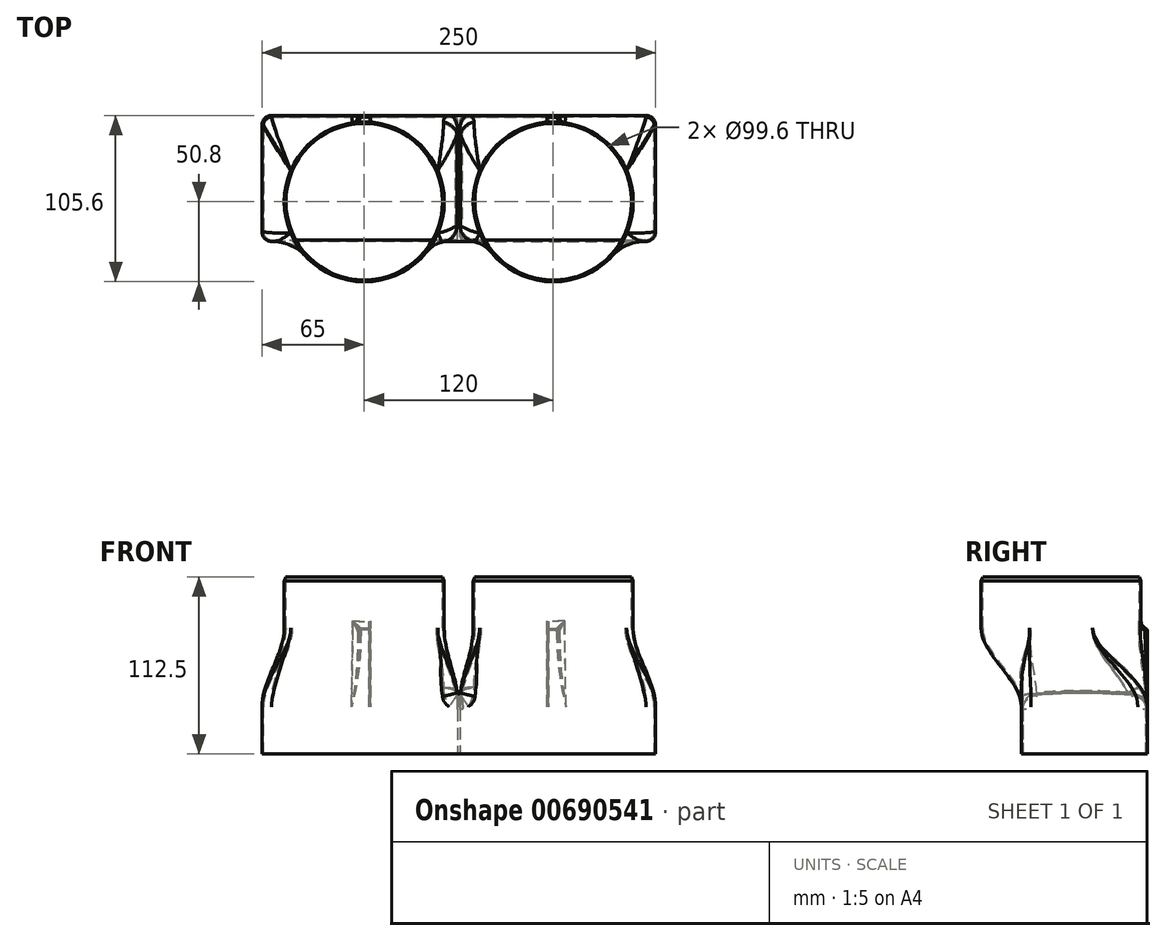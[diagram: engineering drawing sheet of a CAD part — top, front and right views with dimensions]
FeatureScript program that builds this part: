
annotation { "Feature Type Name" : "Feature", "Feature Type Description" : "" }
export const myFeature = defineFeature(function(context is Context, id is Id, definition is map)
    precondition{}
    {
        {
            var Q0;
            Q0=qCreatedBy(makeId("Front.planeOp"),FACE);
            var sketch = newSketch(context, id + "F0", { "sketchPlane" : qUnion([Q0])});
            skLineSegment(sketch, "E0", {"start": v(50.8, 0) * mm, "end": v(50.8, 30) * mm});
            skLineSegment(sketch, "E1", {"start": v(50.8, 30) * mm, "end": v(48.8, 35) * mm});
            skLineSegment(sketch, "E2", {"start": v(48.8, 35) * mm, "end": v(0, 35) * mm});
            skLineSegment(sketch, "E3", {"start": v(0, 35) * mm, "end": v(0, 0) * mm});
            skLineSegment(sketch, "E4", {"start": v(50.8, 0) * mm, "end": v(0, 0) * mm});
            skSolve(sketch);
        }
        {
            var Q0;
            Q0=makeQuery(id+"F0.imprint","IMPRINT",FACE,{"disambiguationData":[TD([[makeQuery(id+"F0.imprint","IMPRINT",EDGE,{"derivedFrom":sQuery(id+"F0.wireOp",EDGE,"E0")}),1.0]])]});
            var Q1;
            Q1=sQuery(id+"F0.wireOp",EDGE,"E3");
            revolve(context, id + "F1", {"entities" : qUnion([Q0]), "axis" : qUnion([Q1]), "revolveType" : RevolveType.FULL});
        }
        {
            var Q0;
            Q0=qCreatedBy(makeId("Right.planeOp"),FACE);
            cPlane(context, id + "F2", {"entities" : qUnion([Q0]), "cplaneType" : CPlaneType.OFFSET, "offset" : 60 * mm, "oppositeDirection" : true, "width" : 150 * mm, "height" : 150 * mm});
        }
        {
            var Q0;
            Q0=qCreatedBy(makeId("Top.planeOp"),FACE);
            cPlane(context, id + "F3", {"entities" : qUnion([Q0]), "cplaneType" : CPlaneType.OFFSET, "offset" : 50 * mm, "oppositeDirection" : true, "width" : 150 * mm, "height" : 150 * mm});
        }
        {
            var Q0;
            Q0=qCreatedBy(id+"F3.planeOp",FACE);
            var sketch = newSketch(context, id + "F4", { "sketchPlane" : qUnion([Q0])});
            skLineSegment(sketch, "E5.bottom", {"start": v(-185, -25.2) * mm, "end": v(65, -25.2) * mm});
            skLineSegment(sketch, "E5.top", {"start": v(-185, 54.8) * mm, "end": v(65, 54.8) * mm});
            skLineSegment(sketch, "E5.left", {"start": v(-185, -25.2) * mm, "end": v(-185, 54.8) * mm});
            skLineSegment(sketch, "E5.right", {"start": v(65, -25.2) * mm, "end": v(65, 54.8) * mm});
            skPoint(sketch, "E5.middle", {"position": v(-60, 14.8) * mm});
            skLineSegment(sketch, "E6", {"start": v(-60, -25.2) * mm, "end": v(-60, 54.8) * mm});
            skSolve(sketch);
        }
        {
            var Q0;
            Q0=qCreatedBy(makeId("Top.planeOp"),FACE);
            var sketch = newSketch(context, id + "F5", { "sketchPlane" : qUnion([Q0])});
            skLineSegment(sketch, "E7.bottom", {"start": v(46.7, -20) * mm, "end": v(-46.7, -20) * mm, "construction": true});
            skLineSegment(sketch, "E7.top", {"start": v(46.7, 20) * mm, "end": v(-46.7, 20) * mm, "construction": true});
            skLineSegment(sketch, "E7.left", {"start": v(46.7, -20) * mm, "end": v(46.7, 20) * mm, "construction": true});
            skLineSegment(sketch, "E7.right", {"start": v(-46.7, -20) * mm, "end": v(-46.7, 20) * mm, "construction": true});
            skPoint(sketch, "E7.middle", {"position": v(0, 0) * mm});
            skArc(sketch, "E8", {"start": v(46.7, -20) * mm, "mid": v(50.8, 0) * mm, "end": v(46.7, 20) * mm});
            skArc(sketch, "E9", {"start": v(46.7, 20) * mm, "mid": v(0, 50.8) * mm, "end": v(-46.7, 20) * mm});
            skArc(sketch, "E10", {"start": v(-46.7, 20) * mm, "mid": v(-50.8, 0) * mm, "end": v(-46.7, -20) * mm});
            skArc(sketch, "E11", {"start": v(-46.7, -20) * mm, "mid": v(0, -50.8) * mm, "end": v(46.7, -20) * mm});
            skSolve(sketch);
        }
        {
            var Q1;
            {var subQ0=sQuery(id+"F4.wireOp",EDGE,"E5.right");Q1=makeQuery(id+"F4.imprint","IMPRINT",FACE,{"disambiguationData":[TD([[makeQuery(id+"F4.imprint","IMPRINT",EDGE,{"derivedFrom":subQ0}),1.0]])]});}
            var Q2;
            Q2 = qSketchRegion(id + "F5", true);
            loft(context, id + "F6", {"operationType" : NewBodyOperationType.ADD, "startCondition" : LoftEndDerivativeType.NORMAL_TO_PROFILE, "startMagnitude" : 1, "endCondition" : LoftEndDerivativeType.NORMAL_TO_PROFILE, "endMagnitude" : 1, "sheetProfilesArray" : [{ "sheetProfileEntities" : qUnion([Q1]) }, { "sheetProfileEntities" : qUnion([Q2]) }]});
        }
        {
            var Q0;
            {var subQ0=sQuery(id+"F4.wireOp",EDGE,"E5.right");Q0=makeQuery(id+"F6.opLoft","CAP_FACE",FACE,{"disambiguationData":[OSD([makeQuery(id+"F4.imprint","IMPRINT",FACE,{"disambiguationData":[TD([[makeQuery(id+"F4.imprint","IMPRINT",EDGE,{"derivedFrom":subQ0}),1.0]])]})])],"isStart":true});}
            extrude(context, id + "F7", {"entities" : qUnion([Q0]), "operationType" : NewBodyOperationType.ADD, "depth" : 30 * mm, "offsetDistance" : 25 * mm});
        }
        {
            var Q0;
            Q0=makeQuery(id+"F7.opExtrude","SWEPT_EDGE",EDGE,{"disambiguationData":[OSD([sQuery(id+"F4.wireOp",EDGE,"E5.bottom"),sQuery(id+"F4.wireOp",EDGE,"E5.right")])]});
            var Q1;
            Q1=makeQuery(id+"F7.opExtrude","SWEPT_EDGE",EDGE,{"disambiguationData":[OSD([sQuery(id+"F4.wireOp",EDGE,"E5.top"),sQuery(id+"F4.wireOp",EDGE,"E5.right")])]});
            fillet(context, id + "F8", {"entities" : qUnion([Q0, Q1]), "radius" : 6 * mm, "tangentPropagation" : true, "allowEdgeOverflow" : false});
        }
        {
            var Q0;
            {var subQ0=makeQuery(id+"F7.opExtrude","SWEPT_FACE",FACE,{"disambiguationData":[OSD([sQuery(id+"F4.wireOp",EDGE,"E5.top"),sQuery(id+"F4.wireOp",EDGE,"E5.right"),sQuery(id+"F4.wireOp",EDGE,"E6")])]});Q0=makeQuery(id+"F15.boolean.opBoolean","MERGE",FACE,{"derivedFrom":[subQ0,makeQuery(id+"F15.opPattern","COPY",FACE,{"derivedFrom":subQ0,"instanceName":"1"})]});}
            var sketch = newSketch(context, id + "F9", { "sketchPlane" : qUnion([Q0])});
            skLineSegment(sketch, "E12.bottom", {"start": v(4, 0) * mm, "end": v(-4, 0) * mm});
            skLineSegment(sketch, "E12.top", {"start": v(4, -50) * mm, "end": v(-4, -50) * mm});
            skLineSegment(sketch, "E12.left", {"start": v(4, 0) * mm, "end": v(4, -50) * mm});
            skLineSegment(sketch, "E12.right", {"start": v(-4, 0) * mm, "end": v(-4, -50) * mm});
            skPoint(sketch, "E12.middle", {"position": v(0, -25) * mm});
            skSolve(sketch);
        }
        {
            var Q0;
            Q0 = qSketchRegion(id + "F9", true);
            var Q1;
            Q1=makeQuery(id+"F6.opLoft","SWEPT_FACE",FACE,{"disambiguationData":[OSD([sQuery(id+"F4.wireOp",EDGE,"E5.top"),sQuery(id+"F4.wireOp",EDGE,"E5.right"),sQuery(id+"F4.wireOp",EDGE,"E6"),sQuery(id+"F5.wireOp",EDGE,"E8"),sQuery(id+"F5.wireOp",EDGE,"E9"),sQuery(id+"F5.wireOp",EDGE,"E10")])]});
            extrude(context, id + "F10", {"entities" : qUnion([Q0]), "operationType" : NewBodyOperationType.ADD, "endBound" : BoundingType.UP_TO_SURFACE, "oppositeDirection" : true, "depth" : 25 * mm, "endBoundEntityFace" : qUnion([Q1]), "offsetDistance" : 25 * mm});
        }
        {
            var Q0;
            Q0=makeQuery(id+"F10.opExtrude","CAP_EDGE",EDGE,{"disambiguationData":[OSD([sQuery(id+"F9.wireOp",EDGE,"E12.bottom")])],"isStart":true});
            fillet(context, id + "F11", {"entities" : qUnion([Q0]), "radius" : 2 * mm, "tangentPropagation" : true, "allowEdgeOverflow" : false});
        }
        {
            var Q0;
            Q0=makeQuery(id+"F10.opExtrude","TWEAK_EDGE",EDGE,{"derivedFrom":[makeQuery(id+"F6.opLoft","SWEPT_FACE",FACE,{"disambiguationData":[OSD([sQuery(id+"F4.wireOp",EDGE,"E5.top"),sQuery(id+"F4.wireOp",EDGE,"E5.right"),sQuery(id+"F4.wireOp",EDGE,"E6"),sQuery(id+"F5.wireOp",EDGE,"E8"),sQuery(id+"F5.wireOp",EDGE,"E9"),sQuery(id+"F5.wireOp",EDGE,"E10")])]}),makeQuery(id+"F9.imprint","IMPRINT",EDGE,{"derivedFrom":sQuery(id+"F9.wireOp",EDGE,"E12.right")})]});
            var Q1;
            Q1=makeQuery(id+"F10.opExtrude","TWEAK_EDGE",EDGE,{"derivedFrom":[makeQuery(id+"F6.opLoft","SWEPT_FACE",FACE,{"disambiguationData":[OSD([sQuery(id+"F4.wireOp",EDGE,"E5.top"),sQuery(id+"F4.wireOp",EDGE,"E5.right"),sQuery(id+"F4.wireOp",EDGE,"E6"),sQuery(id+"F5.wireOp",EDGE,"E8"),sQuery(id+"F5.wireOp",EDGE,"E9"),sQuery(id+"F5.wireOp",EDGE,"E10")])]}),makeQuery(id+"F9.imprint","IMPRINT",EDGE,{"derivedFrom":sQuery(id+"F9.wireOp",EDGE,"E12.left")})]});
            fillet(context, id + "F12", {"entities" : qUnion([Q0, Q1]), "radius" : 4 * mm, "tangentPropagation" : true, "allowEdgeOverflow" : false});
        }
        {
            var Q0;
            {var subQ0=sQuery(id+"F5.wireOp",EDGE,"E10");var subQ1=sQuery(id+"F5.wireOp",EDGE,"E9");var subQ2=sQuery(id+"F5.wireOp",EDGE,"E8");Q0=makeQuery(id+"F10.boolean.opBoolean","MERGE",EDGE,{"derivedFrom":[makeQuery(id+"F6.boolean.opBoolean","MERGE",EDGE,{"derivedFrom":[makeQuery(id+"F1.opRevolve","SWEPT_EDGE",EDGE,{"disambiguationData":[OSD([sQuery(id+"F0.wireOp",EDGE,"E0"),sQuery(id+"F0.wireOp",EDGE,"E4")])]}),makeQuery(id+"F6.opLoft","MID_CAP_EDGE",EDGE,{"disambiguationData":[OSD([subQ2,subQ1,subQ0])],"capPos":1.0})]}),makeQuery(id+"F10.opExtrude","TWEAK_EDGE",EDGE,{"derivedFrom":[makeQuery(id+"F6.opLoft","SWEPT_FACE",FACE,{"disambiguationData":[OSD([sQuery(id+"F4.wireOp",EDGE,"E5.top"),sQuery(id+"F4.wireOp",EDGE,"E5.right"),sQuery(id+"F4.wireOp",EDGE,"E6"),subQ2,subQ1,subQ0])]}),makeQuery(id+"F9.imprint","IMPRINT",EDGE,{"derivedFrom":sQuery(id+"F9.wireOp",EDGE,"E12.bottom")})]})]});}
            fillet(context, id + "F13", {"entities" : qUnion([Q0]), "radius" : 5 * mm, "tangentPropagation" : true, "allowEdgeOverflow" : false});
        }
        {
            var Q0;
            Q0=makeQuery(id+"F12.opFillet","BLEND_EDGE",EDGE,{"blendedFrom":[makeQuery(id+"F10.opExtrude","TWEAK_EDGE",EDGE,{"derivedFrom":[makeQuery(id+"F6.opLoft","SWEPT_FACE",FACE,{"disambiguationData":[OSD([sQuery(id+"F4.wireOp",EDGE,"E5.top"),sQuery(id+"F4.wireOp",EDGE,"E5.right"),sQuery(id+"F4.wireOp",EDGE,"E6"),sQuery(id+"F5.wireOp",EDGE,"E8"),sQuery(id+"F5.wireOp",EDGE,"E9"),sQuery(id+"F5.wireOp",EDGE,"E10")])]}),makeQuery(id+"F9.imprint","IMPRINT",EDGE,{"derivedFrom":sQuery(id+"F9.wireOp",EDGE,"E12.right")})]}),makeQuery(id+"F11.opFillet","BLEND_FACE",FACE,{"disambiguationData":[OSD([sQuery(id+"F9.wireOp",EDGE,"E12.bottom")])]})],"blendedInto":[makeQuery(id+"F11.opFillet","BLEND_FACE",FACE,{"disambiguationData":[OSD([sQuery(id+"F9.wireOp",EDGE,"E12.bottom")])]})]});
            var Q1;
            Q1=makeQuery(id+"F12.opFillet","BLEND_EDGE",EDGE,{"blendedFrom":[makeQuery(id+"F10.opExtrude","TWEAK_EDGE",EDGE,{"derivedFrom":[makeQuery(id+"F6.opLoft","SWEPT_FACE",FACE,{"disambiguationData":[OSD([sQuery(id+"F4.wireOp",EDGE,"E5.top"),sQuery(id+"F4.wireOp",EDGE,"E5.right"),sQuery(id+"F4.wireOp",EDGE,"E6"),sQuery(id+"F5.wireOp",EDGE,"E8"),sQuery(id+"F5.wireOp",EDGE,"E9"),sQuery(id+"F5.wireOp",EDGE,"E10")])]}),makeQuery(id+"F9.imprint","IMPRINT",EDGE,{"derivedFrom":sQuery(id+"F9.wireOp",EDGE,"E12.left")})]}),makeQuery(id+"F11.opFillet","BLEND_FACE",FACE,{"disambiguationData":[OSD([sQuery(id+"F9.wireOp",EDGE,"E12.bottom")])]})],"blendedInto":[makeQuery(id+"F11.opFillet","BLEND_FACE",FACE,{"disambiguationData":[OSD([sQuery(id+"F9.wireOp",EDGE,"E12.bottom")])]})]});
            fillet(context, id + "F14", {"entities" : qUnion([Q0, Q1]), "radius" : 2 * mm, "tangentPropagation" : true, "allowEdgeOverflow" : false});
        }
        {
            var Q0;
            Q0=makeQuery(id+"F1.opRevolve","SWEPT_BODY",BODY,{"disambiguationData":[OSD([sQuery(id+"F0.wireOp",EDGE,"E0"),sQuery(id+"F0.wireOp",EDGE,"E1"),sQuery(id+"F0.wireOp",EDGE,"E2"),sQuery(id+"F0.wireOp",EDGE,"E3"),sQuery(id+"F0.wireOp",EDGE,"E4")])]});
            var Q1;
            Q1=makeQuery(id+"F7.opExtrude","SWEPT_FACE",FACE,{"disambiguationData":[OSD([sQuery(id+"F4.wireOp",EDGE,"E5.bottom"),sQuery(id+"F4.wireOp",EDGE,"E5.top"),sQuery(id+"F4.wireOp",EDGE,"E6")])]});
            mirror(context, id + "F15", {"operationType" : NewBodyOperationType.ADD, "entities" : qUnion([Q0]), "mirrorPlane" : qUnion([Q1])});
        }
        {
            var Q0;
            {var subQ0=sQuery(id+"F4.wireOp",EDGE,"E6");var subQ1=sQuery(id+"F4.wireOp",EDGE,"E5.top");var subQ2=sQuery(id+"F4.wireOp",EDGE,"E5.bottom");var subQ3=makeQuery(id+"F7.boolean.opBoolean","MERGE",EDGE,{"derivedFrom":[makeQuery(id+"F6.opLoft","MID_CAP_EDGE",EDGE,{"disambiguationData":[OSD([subQ2,subQ1,subQ0])],"capPos":0.0}),makeQuery(id+"F7.opExtrude","CAP_EDGE",EDGE,{"disambiguationData":[OSD([subQ2,subQ1,subQ0])],"isStart":true})]});Q0=makeQuery(id+"F15.boolean.opBoolean","MERGE",EDGE,{"derivedFrom":[subQ3,makeQuery(id+"F15.opPattern","COPY",EDGE,{"derivedFrom":subQ3,"instanceName":"1"})]});}
            fillet(context, id + "F16", {"entities" : qUnion([Q0]), "radius" : 1 * mm, "tangentPropagation" : true, "allowEdgeOverflow" : false});
        }
        {
            var Q0;
            Q0=makeQuery(id+"F6.opLoft","SWEPT_EDGE",EDGE,{"disambiguationData":[OSD([sQuery(id+"F4.wireOp",EDGE,"E5.top"),sQuery(id+"F4.wireOp",EDGE,"E6"),sQuery(id+"F5.wireOp",EDGE,"E9"),sQuery(id+"F5.wireOp",EDGE,"E10")])]});
            var Q1;
            Q1=makeQuery(id+"F15.opPattern","COPY",EDGE,{"derivedFrom":makeQuery(id+"F6.opLoft","SWEPT_EDGE",EDGE,{"disambiguationData":[OSD([sQuery(id+"F4.wireOp",EDGE,"E5.top"),sQuery(id+"F4.wireOp",EDGE,"E6"),sQuery(id+"F5.wireOp",EDGE,"E9"),sQuery(id+"F5.wireOp",EDGE,"E10")])]}),"instanceName":"1"});
            var Q2;
            Q2=makeQuery(id+"F6.opLoft","SWEPT_EDGE",EDGE,{"disambiguationData":[OSD([sQuery(id+"F4.wireOp",EDGE,"E5.bottom"),sQuery(id+"F4.wireOp",EDGE,"E6"),sQuery(id+"F5.wireOp",EDGE,"E10"),sQuery(id+"F5.wireOp",EDGE,"E11")])]});
            var Q3;
            Q3=makeQuery(id+"F15.opPattern","COPY",EDGE,{"derivedFrom":makeQuery(id+"F6.opLoft","SWEPT_EDGE",EDGE,{"disambiguationData":[OSD([sQuery(id+"F4.wireOp",EDGE,"E5.bottom"),sQuery(id+"F4.wireOp",EDGE,"E6"),sQuery(id+"F5.wireOp",EDGE,"E10"),sQuery(id+"F5.wireOp",EDGE,"E11")])]}),"instanceName":"1"});
            fillet(context, id + "F17", {"entities" : qUnion([Q0, Q1, Q2, Q3]), "radius" : 10 * mm, "tangentPropagation" : true, "allowEdgeOverflow" : false});
        }
        {
            var Q0;
            {var subQ0=sQuery(id+"F4.wireOp",EDGE,"E5.right");var subQ4=makeQuery(id+"F7.opExtrude","CAP_FACE",FACE,{"disambiguationData":[OSD([makeQuery(id+"F4.imprint","IMPRINT",FACE,{"disambiguationData":[TD([[makeQuery(id+"F4.imprint","IMPRINT",EDGE,{"derivedFrom":subQ0}),1.0]])]})])],"isStart":false});Q0=makeQuery(id+"F15.boolean.opBoolean","MERGE",FACE,{"derivedFrom":[subQ4,makeQuery(id+"F15.opPattern","COPY",FACE,{"derivedFrom":subQ4,"instanceName":"1"})]});}
            var Q1;
            Q1=makeQuery(id+"F1.opRevolve","SWEPT_FACE",FACE,{"disambiguationData":[OSD([sQuery(id+"F0.wireOp",EDGE,"E2")])]});
            var Q2;
            Q2=makeQuery(id+"F15.opPattern","COPY",FACE,{"derivedFrom":makeQuery(id+"F1.opRevolve","SWEPT_FACE",FACE,{"disambiguationData":[OSD([sQuery(id+"F0.wireOp",EDGE,"E2")])]}),"instanceName":"1"});
            var Q3;
            Q3=makeQuery(id+"F15.opPattern","COPY",FACE,{"derivedFrom":makeQuery(id+"F1.opRevolve","SWEPT_FACE",FACE,{"disambiguationData":[OSD([sQuery(id+"F0.wireOp",EDGE,"E1")])]}),"instanceName":"1"});
            var Q4;
            Q4=makeQuery(id+"F1.opRevolve","SWEPT_FACE",FACE,{"disambiguationData":[OSD([sQuery(id+"F0.wireOp",EDGE,"E1")])]});
            shell(context, id + "F18", {"entities" : qUnion([Q0, Q1, Q2, Q3, Q4]), "thickness" : 1 * mm});
        }
        {
            var Q0;
            {var subQ0=sQuery(id+"F4.wireOp",EDGE,"E5.right");var subQ4=makeQuery(id+"F7.opExtrude","CAP_FACE",FACE,{"disambiguationData":[OSD([makeQuery(id+"F4.imprint","IMPRINT",FACE,{"disambiguationData":[TD([[makeQuery(id+"F4.imprint","IMPRINT",EDGE,{"derivedFrom":subQ0}),1.0]])]})])],"isStart":false});Q0=makeQuery(id+"F15.boolean.opBoolean","MERGE",FACE,{"derivedFrom":[subQ4,makeQuery(id+"F15.opPattern","COPY",FACE,{"derivedFrom":subQ4,"instanceName":"1"})]});}
            var sketch = newSketch(context, id + "F19", { "sketchPlane" : qUnion([Q0])});
            skLineSegment(sketch, "E13.bottom", {"start": v(-60.75, 24.2) * mm, "end": v(-59.25, 24.2) * mm});
            skLineSegment(sketch, "E13.top", {"start": v(-60.75, -53.8) * mm, "end": v(-59.25, -53.8) * mm});
            skLineSegment(sketch, "E13.left", {"start": v(-60.75, 24.2) * mm, "end": v(-60.75, -53.8) * mm});
            skLineSegment(sketch, "E13.right", {"start": v(-59.25, 24.2) * mm, "end": v(-59.25, -53.8) * mm});
            skPoint(sketch, "E13.middle", {"position": v(-60, -14.8) * mm});
            skPoint(sketch, "E13.middle.positionSnap0", {"position": v(-60, 24.2) * mm});
            skPoint(sketch, "E13.centerSnap0", {"position": v(-60, 24.2) * mm});
            skSolve(sketch);
        }
        {
            var Q0;
            Q0 = qSketchRegion(id + "F19", true);
            var Q1;
            Q1=makeQuery(id+"F1.opRevolve","SWEPT_BODY",BODY,{"disambiguationData":[OSD([sQuery(id+"F0.wireOp",EDGE,"E0"),sQuery(id+"F0.wireOp",EDGE,"E1"),sQuery(id+"F0.wireOp",EDGE,"E2"),sQuery(id+"F0.wireOp",EDGE,"E3"),sQuery(id+"F0.wireOp",EDGE,"E4")])]});
            extrude(context, id + "F20", {"entities" : qUnion([Q0]), "operationType" : NewBodyOperationType.ADD, "endBound" : BoundingType.UP_TO_BODY, "oppositeDirection" : true, "depth" : 25 * mm, "endBoundEntityBody" : qUnion([Q1]), "offsetDistance" : 25 * mm});
        }
        {
            var Q0;
            Q0=makeQuery(id+"F20.opExtrude","SWEPT_EDGE",EDGE,{"disambiguationData":[OSD([sQuery(id+"F4.wireOp",EDGE,"E5.bottom"),sQuery(id+"F4.wireOp",EDGE,"E5.right"),sQuery(id+"F4.wireOp",EDGE,"E6"),sQuery(id+"F19.wireOp",EDGE,"E13.bottom"),sQuery(id+"F19.wireOp",EDGE,"E13.left")])]});
            var Q1;
            Q1=makeQuery(id+"F20.opExtrude","SWEPT_EDGE",EDGE,{"disambiguationData":[OSD([sQuery(id+"F4.wireOp",EDGE,"E5.bottom"),sQuery(id+"F4.wireOp",EDGE,"E5.right"),sQuery(id+"F4.wireOp",EDGE,"E6"),sQuery(id+"F19.wireOp",EDGE,"E13.bottom"),sQuery(id+"F19.wireOp",EDGE,"E13.right")])]});
            fillet(context, id + "F21", {"entities" : qUnion([Q0, Q1]), "radius" : 2 * mm, "tangentPropagation" : true, "allowEdgeOverflow" : false});
        }
    });
